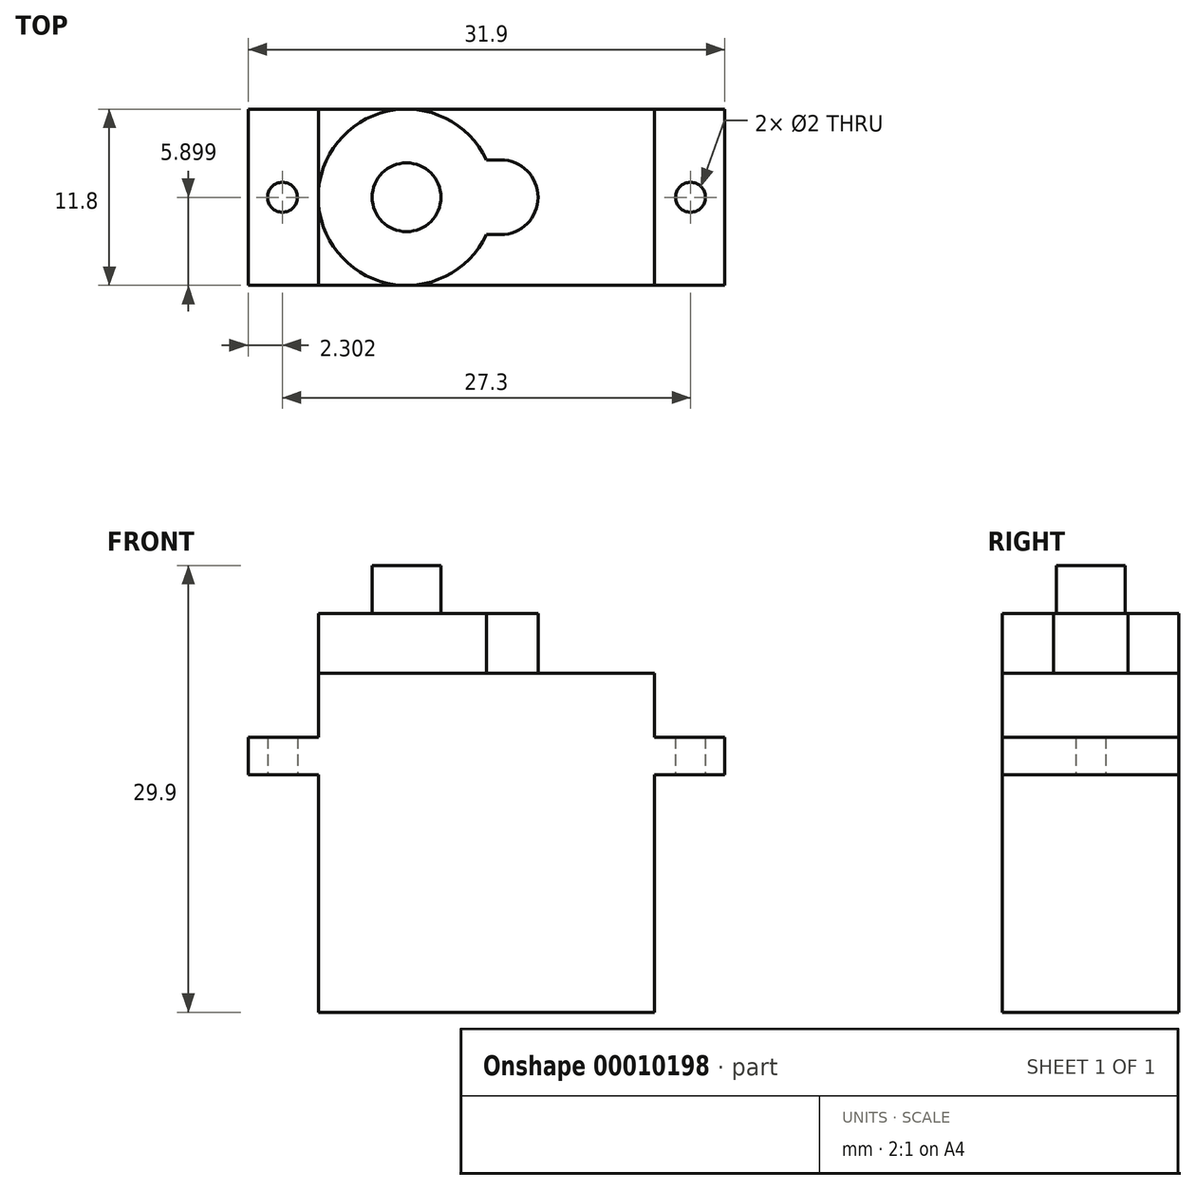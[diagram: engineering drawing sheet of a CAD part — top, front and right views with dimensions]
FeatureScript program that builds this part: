
annotation { "Feature Type Name" : "Feature", "Feature Type Description" : "" }
export const myFeature = defineFeature(function(context is Context, id is Id, definition is map)
    precondition{}
    {
        {
            var Q0;
            Q0=qCreatedBy(makeId("Top.planeOp"),FACE);
            var sketch = newSketch(context, id + "F0", { "sketchPlane" : qUnion([Q0])});
            skLineSegment(sketch, "E0.bottom", {"start": v(-20.09, -19.97) * mm, "end": v(2.41, -19.97) * mm});
            skLineSegment(sketch, "E0.top", {"start": v(-20.09, -31.77) * mm, "end": v(2.41, -31.77) * mm});
            skLineSegment(sketch, "E0.left", {"start": v(-20.09, -19.97) * mm, "end": v(-20.09, -31.77) * mm});
            skLineSegment(sketch, "E0.right", {"start": v(2.41, -19.97) * mm, "end": v(2.41, -31.77) * mm});
            skSolve(sketch);
        }
        {
            var Q0;
            Q0 = qSketchRegion(id + "F0", true);
            extrude(context, id + "F1", {"entities" : qUnion([Q0]), "depth" : 15.9 * mm});
        }
        {
            var Q0;
            Q0=makeQuery(id+"F1.opExtrude","CAP_FACE",FACE,{"disambiguationData":[OSD([sQuery(id+"F0.wireOp",EDGE,"E0.bottom"),sQuery(id+"F0.wireOp",EDGE,"E0.top"),sQuery(id+"F0.wireOp",EDGE,"E0.left"),sQuery(id+"F0.wireOp",EDGE,"E0.right")])],"isStart":false});
            var sketch = newSketch(context, id + "F2", { "sketchPlane" : qUnion([Q0])});
            skLineSegment(sketch, "E1.bottom", {"start": v(7.11, -31.77) * mm, "end": v(-24.79, -31.77) * mm});
            skLineSegment(sketch, "E1.top", {"start": v(7.11, -19.97) * mm, "end": v(-24.79, -19.97) * mm});
            skLineSegment(sketch, "E1.left", {"start": v(7.11, -31.77) * mm, "end": v(7.11, -19.97) * mm});
            skLineSegment(sketch, "E1.right", {"start": v(-24.79, -31.77) * mm, "end": v(-24.79, -19.97) * mm});
            skCircle(sketch, "E2", {"center": v(-22.49, -25.87) * mm, "radius": 1 * mm});
            skCircle(sketch, "E3", {"center": v(4.81, -25.87) * mm, "radius": 1 * mm});
            skSolve(sketch);
        }
        {
            var Q0;
            Q0 = qSketchRegion(id + "F2", true);
            extrude(context, id + "F3", {"entities" : qUnion([Q0]), "operationType" : NewBodyOperationType.ADD, "depth" : 2.5 * mm});
        }
        {
            var Q0;
            Q0=makeQuery(id+"F3.opExtrude","CAP_FACE",FACE,{"disambiguationData":[OSD([sQuery(id+"F2.wireOp",EDGE,"E1.bottom"),sQuery(id+"F2.wireOp",EDGE,"E1.top"),sQuery(id+"F2.wireOp",EDGE,"E1.left"),sQuery(id+"F2.wireOp",EDGE,"E1.right"),sQuery(id+"F2.wireOp",EDGE,"E2"),sQuery(id+"F2.wireOp",EDGE,"E3")])],"isStart":false});
            var sketch = newSketch(context, id + "F4", { "sketchPlane" : qUnion([Q0])});
            skLineSegment(sketch, "E4.bottom", {"start": v(-20.09, -31.77) * mm, "end": v(2.41, -31.77) * mm});
            skLineSegment(sketch, "E4.top", {"start": v(-20.09, -19.97) * mm, "end": v(2.41, -19.97) * mm});
            skLineSegment(sketch, "E4.left", {"start": v(-20.09, -31.77) * mm, "end": v(-20.09, -19.97) * mm});
            skLineSegment(sketch, "E4.right", {"start": v(2.41, -31.77) * mm, "end": v(2.41, -19.97) * mm});
            skSolve(sketch);
        }
        {
            var Q0;
            Q0 = qSketchRegion(id + "F4", true);
            extrude(context, id + "F5", {"entities" : qUnion([Q0]), "operationType" : NewBodyOperationType.ADD, "depth" : 4.3 * mm});
        }
        {
            var Q0;
            Q0=makeQuery(id+"F5.opExtrude","CAP_FACE",FACE,{"disambiguationData":[OSD([sQuery(id+"F4.wireOp",EDGE,"E4.bottom"),sQuery(id+"F4.wireOp",EDGE,"E4.top"),sQuery(id+"F4.wireOp",EDGE,"E4.left"),sQuery(id+"F4.wireOp",EDGE,"E4.right")])],"isStart":false});
            var sketch = newSketch(context, id + "F6", { "sketchPlane" : qUnion([Q0])});
            skArc(sketch, "E5", {"start": v(-8.84, -23.37) * mm, "mid": v(-20.09, -25.87) * mm, "end": v(-8.84, -28.37) * mm});
            skArc(sketch, "E6", {"start": v(-7.89, -28.37) * mm, "mid": v(-5.39, -25.87) * mm, "end": v(-7.89, -23.37) * mm});
            skLineSegment(sketch, "E7", {"start": v(-7.89, -28.37) * mm, "end": v(-8.84, -28.37) * mm});
            skLineSegment(sketch, "E8", {"start": v(-7.89, -23.37) * mm, "end": v(-8.84, -23.37) * mm});
            skSolve(sketch);
        }
        {
            var Q0;
            Q0 = qSketchRegion(id + "F6", true);
            extrude(context, id + "F7", {"entities" : qUnion([Q0]), "operationType" : NewBodyOperationType.ADD, "depth" : 4 * mm});
        }
        {
            var Q0;
            Q0=makeQuery(id+"F7.opExtrude","CAP_FACE",FACE,{"disambiguationData":[OSD([sQuery(id+"F6.wireOp",EDGE,"E5"),sQuery(id+"F6.wireOp",EDGE,"E6"),sQuery(id+"F6.wireOp",EDGE,"E7"),sQuery(id+"F6.wireOp",EDGE,"E8")])],"isStart":false});
            var sketch = newSketch(context, id + "F8", { "sketchPlane" : qUnion([Q0])});
            skCircle(sketch, "E9", {"center": v(-14.19, -25.87) * mm, "radius": 2.3 * mm});
            skSolve(sketch);
        }
        {
            var Q0;
            Q0 = qSketchRegion(id + "F8", true);
            extrude(context, id + "F9", {"entities" : qUnion([Q0]), "operationType" : NewBodyOperationType.ADD, "depth" : 3.2 * mm});
        }
    });
